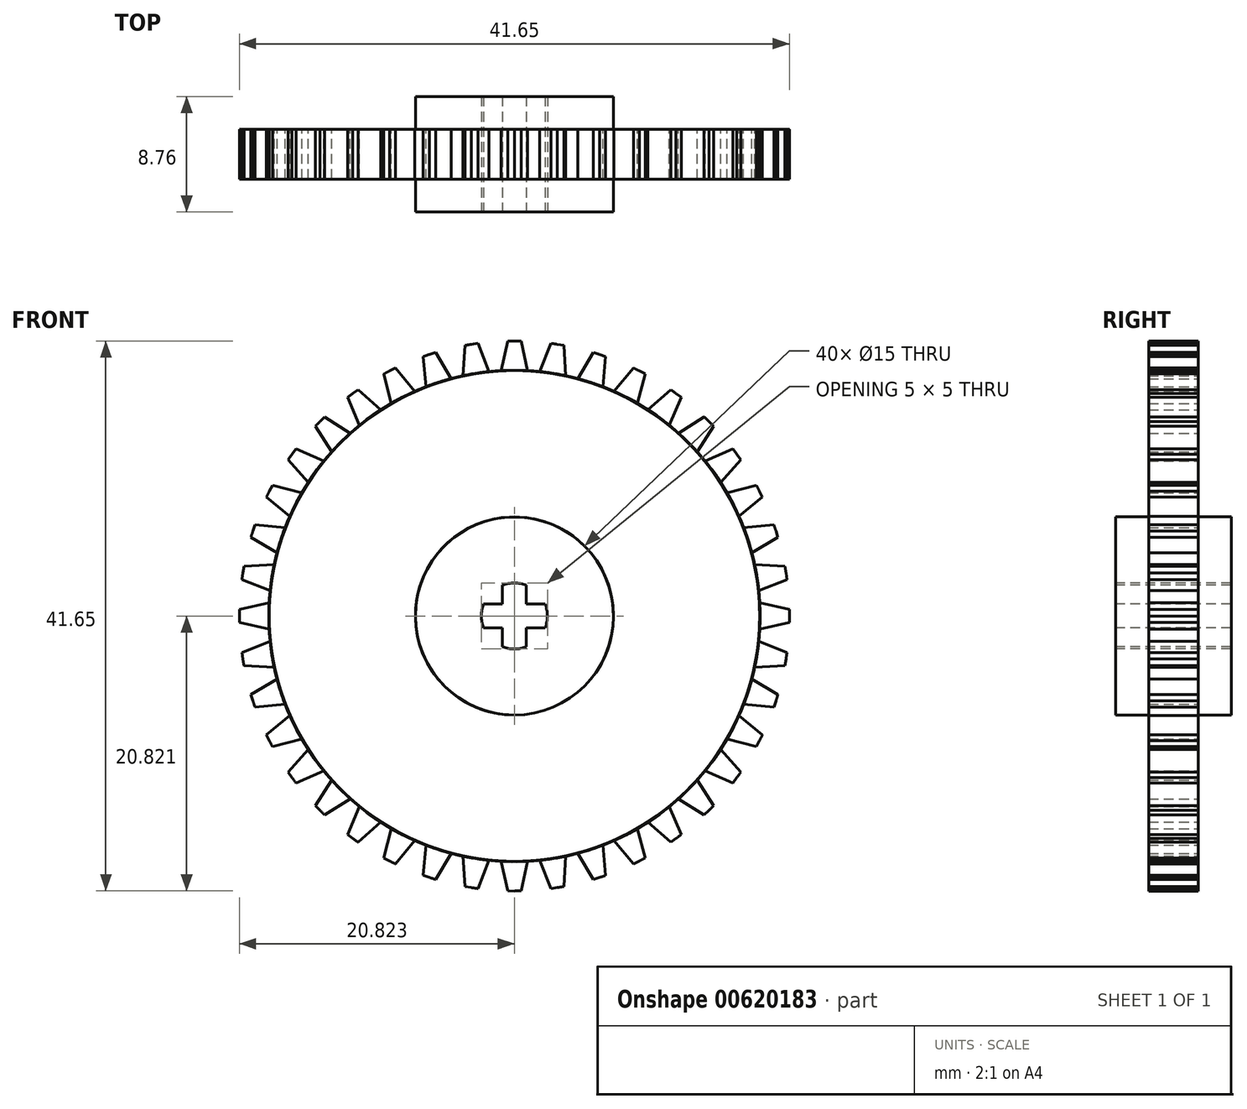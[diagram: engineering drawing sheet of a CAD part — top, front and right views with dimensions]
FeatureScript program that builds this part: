
annotation { "Feature Type Name" : "Feature", "Feature Type Description" : "" }
export const myFeature = defineFeature(function(context is Context, id is Id, definition is map)
    precondition{}
    {
        {
            var Q0;
            Q0=qCreatedBy(makeId("Front.planeOp"),FACE);
            var sketch = newSketch(context, id + "F0", { "sketchPlane" : qUnion([Q0])});
            skArc(sketch, "E0", {"start": v(0.3, 5.55) * mm, "mid": v(-0.2, 5.56) * mm, "end": v(-0.7, 5.55) * mm});
            skCircle(sketch, "E1", {"center": v(-0.2, -15.27) * mm, "radius": 18.6 * mm});
            skLineSegment(sketch, "E2", {"start": v(-0.2, 5.56) * mm, "end": v(-0.2, 3.33) * mm, "construction": true});
            skLineSegment(sketch, "E3", {"start": v(-0.2, 3.33) * mm, "end": v(-0.2, 0.53) * mm, "construction": true});
            skLineSegment(sketch, "E4", {"start": v(-1.2, 3.3) * mm, "end": v(-0.2, 3.3) * mm, "construction": true});
            skLineSegment(sketch, "E5", {"start": v(-0.2, 3.3) * mm, "end": v(0.8, 3.3) * mm, "construction": true});
            skLineSegment(sketch, "E6", {"start": v(0.79, 3.37) * mm, "end": v(0.84, 3.16) * mm});
            skLineSegment(sketch, "E7", {"start": v(-1.17, 3.42) * mm, "end": v(-1.23, 3.15) * mm});
            skLineSegment(sketch, "E8", {"start": v(0.3, 5.55) * mm, "end": v(0.82, 3.23) * mm});
            skLineSegment(sketch, "E9", {"start": v(-1.21, 3.23) * mm, "end": v(-0.7, 5.55) * mm});
            skCircle(sketch, "E10", {"center": v(-0.2, -15.27) * mm, "radius": 7.5 * mm});
            skLineSegment(sketch, "E11", {"start": v(-0.2, -15.27) * mm, "end": v(-0.2, 3.3) * mm, "construction": true});
            skLineSegment(sketch, "E12", {"start": v(-0.2, 5.56) * mm, "end": v(0.3, 5.55) * mm});
            skSolve(sketch);
        }
        {
            var Q0;
            {var subQ5=sQuery(id+"F0.wireOp",EDGE,"E12");Q0=makeQuery(id+"F0.imprint","IMPRINT",FACE,{"disambiguationData":[TD([[makeQuery(id+"F0.imprint","IMPRINT",EDGE,{"derivedFrom":subQ5}),-1.0]])]});}
            var Q1;
            Q1=makeQuery(id+"F0.imprint","IMPRINT",FACE,{"disambiguationData":[TD([[makeQuery(id+"F0.imprint","IMPRINT",EDGE,{"derivedFrom":sQuery(id+"F0.wireOp",EDGE,"E10")}),-1.0]])]});
            extrude(context, id + "F1", {"entities" : qUnion([Q0, Q1]), "endBound" : BoundingType.SYMMETRIC, "depth" : 3.75 * mm, "offsetDistance" : 25 * mm});
        }
        {
            var Q0;
            Q0=makeQuery(id+"F1.opExtrude","CAP_FACE",FACE,{"disambiguationData":[OSD([sQuery(id+"F0.wireOp",EDGE,"E0"),sQuery(id+"F0.wireOp",EDGE,"E1"),sQuery(id+"F0.wireOp",EDGE,"E8"),sQuery(id+"F0.wireOp",EDGE,"E9"),sQuery(id+"F0.wireOp",EDGE,"E10"),sQuery(id+"F0.wireOp",EDGE,"E12")])],"isStart":true});
            var sketch = newSketch(context, id + "F2", { "sketchPlane" : qUnion([Q0])});
            skCircle(sketch, "E13", {"center": v(0.2, -15.27) * mm, "radius": 18.6 * mm});
            skLineSegment(sketch, "E14", {"start": v(0.95, 4.43) * mm, "end": v(0.7, 5.55) * mm});
            skSolve(sketch);
        }
        {
            var Q0;
            Q0=makeQuery(id+"F1.opExtrude","SWEPT_BODY",BODY,{"disambiguationData":[OSD([sQuery(id+"F0.wireOp",EDGE,"E0"),sQuery(id+"F0.wireOp",EDGE,"E1"),sQuery(id+"F0.wireOp",EDGE,"E8"),sQuery(id+"F0.wireOp",EDGE,"E9"),sQuery(id+"F0.wireOp",EDGE,"E10"),sQuery(id+"F0.wireOp",EDGE,"E12")])]});
            var Q1;
            Q1=sQuery(id+"F2.wireOp",EDGE,"E13");
            circularPattern(context, id + "F3", {"entities" : qUnion([Q0]), "axis" : qUnion([Q1]), "angle" : 360 * degree, "instanceCount" : 40, "equalSpace" : true});
        }
        {
            var Q0;
            Q0=makeQuery(id+"F0.imprint","IMPRINT",FACE,{"disambiguationData":[TD([[makeQuery(id+"F0.imprint","IMPRINT",EDGE,{"derivedFrom":sQuery(id+"F0.wireOp",EDGE,"E10")}),1.0]])]});
            extrude(context, id + "F4", {"entities" : qUnion([Q0]), "endBound" : BoundingType.SYMMETRIC, "depth" : 8.75 * mm, "offsetDistance" : 25 * mm});
        }
        {
            var Q0;
            Q0=makeQuery(id+"F4.opExtrude","CAP_FACE",FACE,{"disambiguationData":[OSD([sQuery(id+"F0.wireOp",EDGE,"E10")])],"isStart":false});
            var sketch = newSketch(context, id + "F5", { "sketchPlane" : qUnion([Q0])});
            skCircle(sketch, "E15", {"center": v(-0.2, -15.27) * mm, "radius": 2.5 * mm});
            skLineSegment(sketch, "E16", {"start": v(-1.1, -12.94) * mm, "end": v(-1.1, -14.37) * mm});
            skLineSegment(sketch, "E17", {"start": v(0.7, -14.37) * mm, "end": v(0.7, -12.94) * mm});
            skLineSegment(sketch, "E18", {"start": v(0.7, -14.37) * mm, "end": v(2.13, -14.37) * mm});
            skLineSegment(sketch, "E19", {"start": v(2.13, -16.17) * mm, "end": v(0.7, -16.17) * mm});
            skLineSegment(sketch, "E20", {"start": v(0.7, -16.17) * mm, "end": v(0.7, -17.6) * mm});
            skLineSegment(sketch, "E21", {"start": v(-1.1, -14.37) * mm, "end": v(-2.53, -14.37) * mm});
            skLineSegment(sketch, "E22", {"start": v(-1.1, -17.6) * mm, "end": v(-1.1, -16.17) * mm});
            skLineSegment(sketch, "E23", {"start": v(-2.53, -16.17) * mm, "end": v(-1.1, -16.17) * mm});
            skSolve(sketch);
        }
        {
            var Q0;
            {var subQ4=sQuery(id+"F5.wireOp",EDGE,"E16");Q0=makeQuery(id+"F5.imprint","IMPRINT",FACE,{"disambiguationData":[TD([[makeQuery(id+"F5.imprint","IMPRINT",EDGE,{"derivedFrom":subQ4}),1.0]])]});}
            extrude(context, id + "F6", {"entities" : qUnion([Q0]), "operationType" : NewBodyOperationType.REMOVE, "oppositeDirection" : true, "depth" : 25 * mm, "offsetDistance" : 25 * mm});
        }
    });
